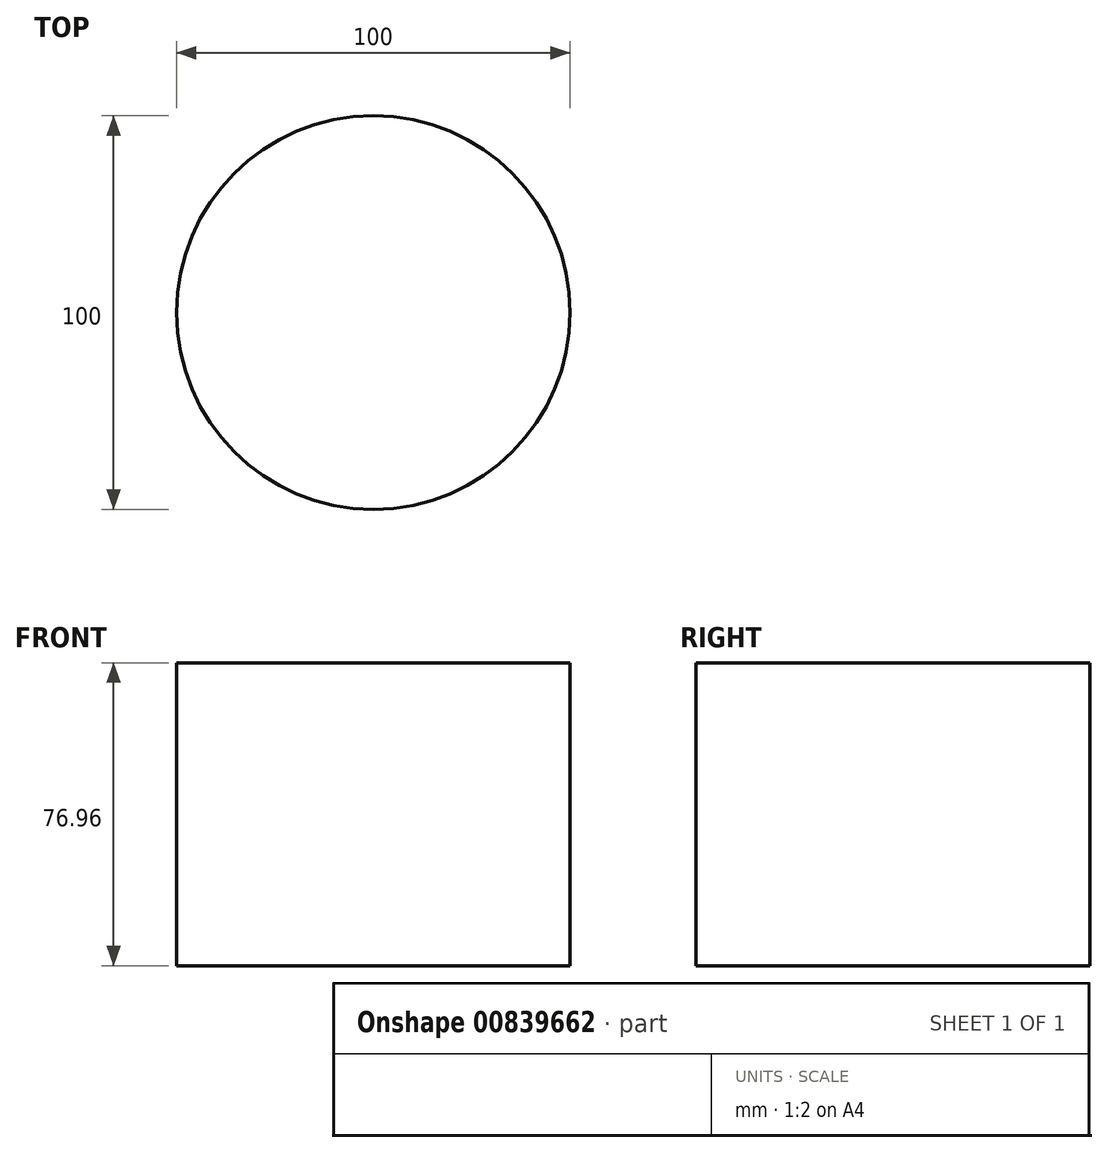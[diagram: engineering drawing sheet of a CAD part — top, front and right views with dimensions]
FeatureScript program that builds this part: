
annotation { "Feature Type Name" : "Feature", "Feature Type Description" : "" }
export const myFeature = defineFeature(function(context is Context, id is Id, definition is map)
    precondition{}
    {
        {
            var Q0;
            Q0=qCreatedBy(makeId("Top.planeOp"),FACE);
            var sketch = newSketch(context, id + "F0", { "sketchPlane" : qUnion([Q0])});
            skCircle(sketch, "E0", {"center": v(0, 0) * mm, "radius": 50 * mm});
            skSolve(sketch);
        }
        {
            var Q0;
            Q0=makeQuery(id+"F0.imprint","IMPRINT",FACE,{"disambiguationData":[TD([[makeQuery(id+"F0.imprint","IMPRINT",EDGE,{"derivedFrom":sQuery(id+"F0.wireOp",EDGE,"E0")}),1.0]])]});
            extrude(context, id + "F1", {"entities" : qUnion([Q0]), "depth" : 76.96 * mm, "offsetDistance" : 25.4 * mm});
        }
    });
